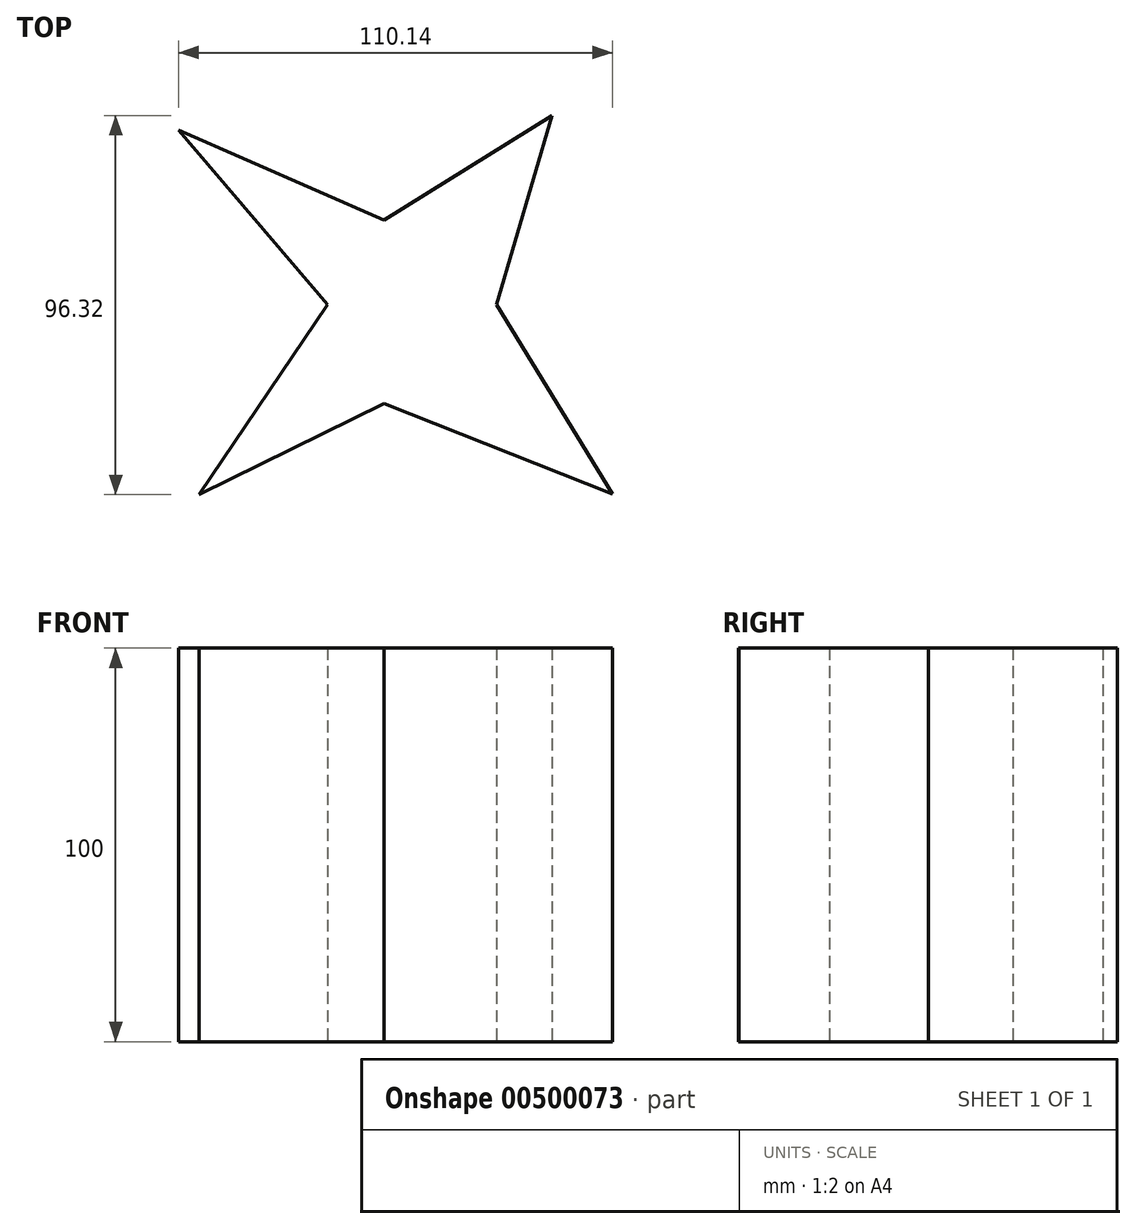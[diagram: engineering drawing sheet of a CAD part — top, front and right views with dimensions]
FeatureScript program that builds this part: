
annotation { "Feature Type Name" : "Feature", "Feature Type Description" : "" }
export const myFeature = defineFeature(function(context is Context, id is Id, definition is map)
    precondition{}
    {
        {
            var Q0;
            Q0=qCreatedBy(makeId("Top.planeOp"),FACE);
            var sketch = newSketch(context, id + "F0", { "sketchPlane" : qUnion([Q0])});
            skLineSegment(sketch, "E0", {"start": v(0, 21.49) * mm, "end": v(42.67, 48) * mm});
            skLineSegment(sketch, "E1", {"start": v(42.67, 48) * mm, "end": v(28.65, 0) * mm});
            skLineSegment(sketch, "E2", {"start": v(28.65, 0) * mm, "end": v(58.14, -48.31) * mm});
            skLineSegment(sketch, "E3", {"start": v(58.52, -48.31) * mm, "end": v(0, -25.15) * mm});
            skLineSegment(sketch, "E4", {"start": v(0, -25.15) * mm, "end": v(-46.94, -48.31) * mm});
            skLineSegment(sketch, "E5", {"start": v(-46.94, -48.31) * mm, "end": v(-14.33, 0) * mm});
            skLineSegment(sketch, "E6", {"start": v(-14.33, 0) * mm, "end": v(-52.12, 44.35) * mm});
            skLineSegment(sketch, "E7", {"start": v(-52.12, 44.35) * mm, "end": v(0, 21.49) * mm});
            skSolve(sketch);
        }
        {
            var Q0;
            Q0=makeQuery(id+"F0.imprint","IMPRINT",FACE,{"disambiguationData":[TD([[makeQuery(id+"F0.imprint","IMPRINT",EDGE,{"derivedFrom":sQuery(id+"F0.wireOp",EDGE,"E0")}),-1.0]])]});
            extrude(context, id + "F1", {"entities" : qUnion([Q0]), "endBound" : BoundingType.SYMMETRIC, "depth" : 100 * mm});
        }
    });
